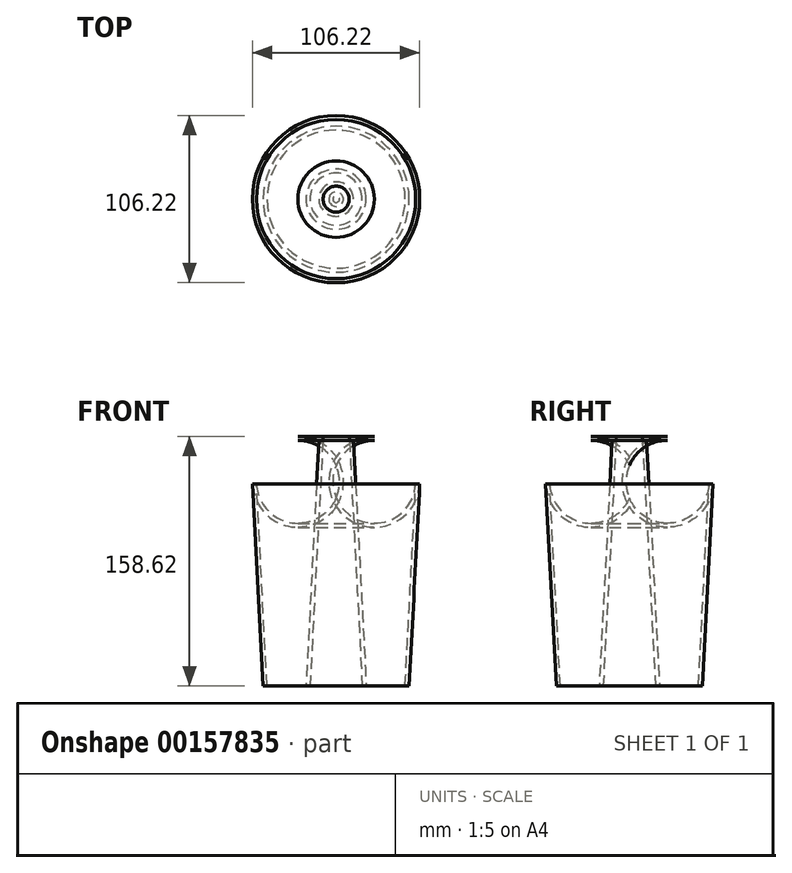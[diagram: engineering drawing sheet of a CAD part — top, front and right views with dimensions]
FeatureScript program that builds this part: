
annotation { "Feature Type Name" : "Feature", "Feature Type Description" : "" }
export const myFeature = defineFeature(function(context is Context, id is Id, definition is map)
    precondition{}
    {
        {
            var Q0;
            Q0=qCreatedBy(makeId("Top.planeOp"),FACE);
            var sketch = newSketch(context, id + "F0", { "sketchPlane" : qUnion([Q0])});
            skCircle(sketch, "E0", {"center": v(-177.56, -11.33) * mm, "radius": 43.85 * mm});
            skCircle(sketch, "E1", {"center": v(-177.56, -11.33) * mm, "radius": 19.14 * mm});
            skSolve(sketch);
        }
        {
            var Q0;
            Q0 = qSketchRegion(id + "F0", true);
            extrude(context, id + "F1", {"entities" : qUnion([Q0]), "depth" : 99.7 * mm, "hasDraft" : true, "draftAngle" : 3 * degree});
        }
        {
            var Q0;
            Q0=makeQuery(id+"F1.opExtrude","CAP_FACE",FACE,{"disambiguationData":[OSD([sQuery(id+"F0.wireOp",EDGE,"E0")])],"isStart":false});
            extrude(context, id + "F2", {"entities" : qUnion([Q0]), "operationType" : NewBodyOperationType.ADD, "depth" : 56.4 * mm, "hasDraft" : true, "draftAngle" : 3 * degree});
        }
        {
            var Q0;
            Q0=makeQuery(id+"F2.opExtrude","CAP_EDGE",EDGE,{"disambiguationData":[OSD([sQuery(id+"F0.wireOp",EDGE,"E0")])],"isStart":false});
            fillet(context, id + "F3", {"entities" : qUnion([Q0]), "radius" : 26.37 * mm, "tangentPropagation" : true, "allowEdgeOverflow" : false});
        }
        {
            var Q0;
            Q0=makeQuery(id+"F1.opExtrude","CAP_FACE",FACE,{"disambiguationData":[OSD([sQuery(id+"F0.wireOp",EDGE,"E0")])],"isStart":true});
            shell(context, id + "F4", {"entities" : qUnion([Q0]), "thickness" : 2.54 * mm, "oppositeDirection" : true});
        }
    });
